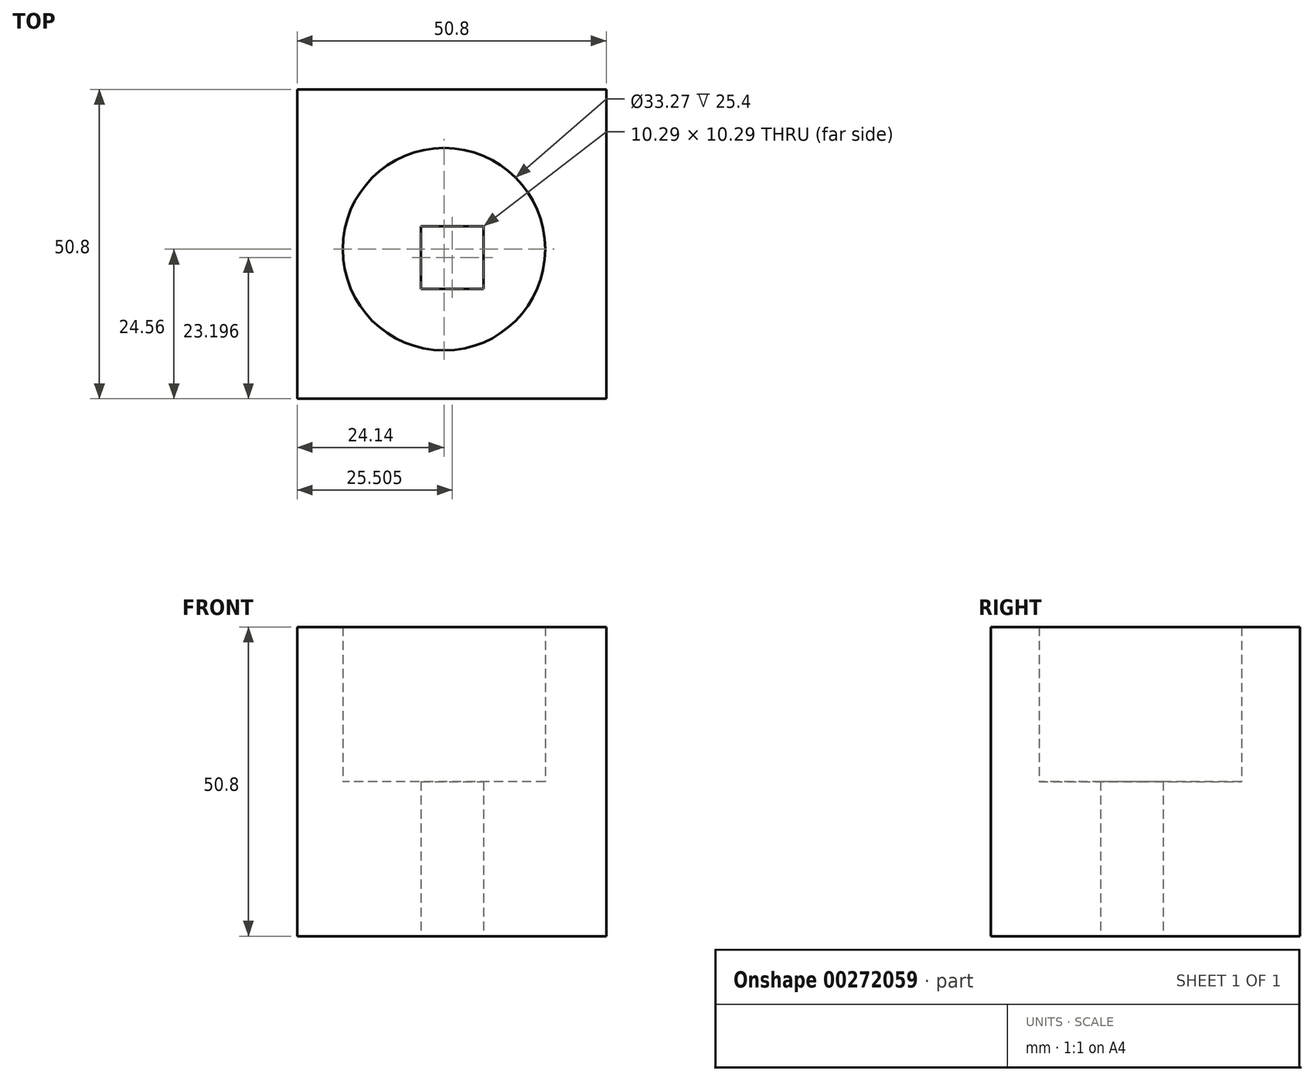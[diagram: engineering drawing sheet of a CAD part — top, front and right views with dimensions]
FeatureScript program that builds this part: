
annotation { "Feature Type Name" : "Feature", "Feature Type Description" : "" }
export const myFeature = defineFeature(function(context is Context, id is Id, definition is map)
    precondition{}
    {
        {
            var Q0;
            Q0=qCreatedBy(makeId("Top.planeOp"),FACE);
            var sketch = newSketch(context, id + "F0", { "sketchPlane" : qUnion([Q0])});
            skLineSegment(sketch, "E0.bottom", {"start": v(0, 0) * mm, "end": v(50.8, 0) * mm});
            skLineSegment(sketch, "E0.top", {"start": v(0, 50.8) * mm, "end": v(50.8, 50.8) * mm});
            skLineSegment(sketch, "E0.left", {"start": v(0, 0) * mm, "end": v(0, 50.8) * mm});
            skLineSegment(sketch, "E0.right", {"start": v(50.8, 0) * mm, "end": v(50.8, 50.8) * mm});
            skCircle(sketch, "E1", {"center": v(24.14, 24.56) * mm, "radius": 16.64 * mm});
            skLineSegment(sketch, "E2.bottom", {"start": v(20.36, 28.34) * mm, "end": v(30.65, 28.34) * mm});
            skLineSegment(sketch, "E2.top", {"start": v(20.36, 18.05) * mm, "end": v(30.65, 18.05) * mm});
            skLineSegment(sketch, "E2.left", {"start": v(20.36, 28.34) * mm, "end": v(20.36, 18.05) * mm});
            skLineSegment(sketch, "E2.right", {"start": v(30.65, 28.34) * mm, "end": v(30.65, 18.05) * mm});
            skSolve(sketch);
        }
        {
            var Q0;
            Q0=makeQuery(id+"F0.imprint","IMPRINT",FACE,{"disambiguationData":[TD([[makeQuery(id+"F0.imprint","IMPRINT",EDGE,{"derivedFrom":sQuery(id+"F0.wireOp",EDGE,"E1")}),1.0]])]});
            extrude(context, id + "F1", {"entities" : qUnion([Q0]), "depth" : 25.4 * mm});
        }
        {
            var Q0;
            Q0 = qSketchRegion(id + "F0", true);
            extrude(context, id + "F2", {"entities" : qUnion([Q0]), "operationType" : NewBodyOperationType.ADD, "depth" : 50.8 * mm});
        }
    });
